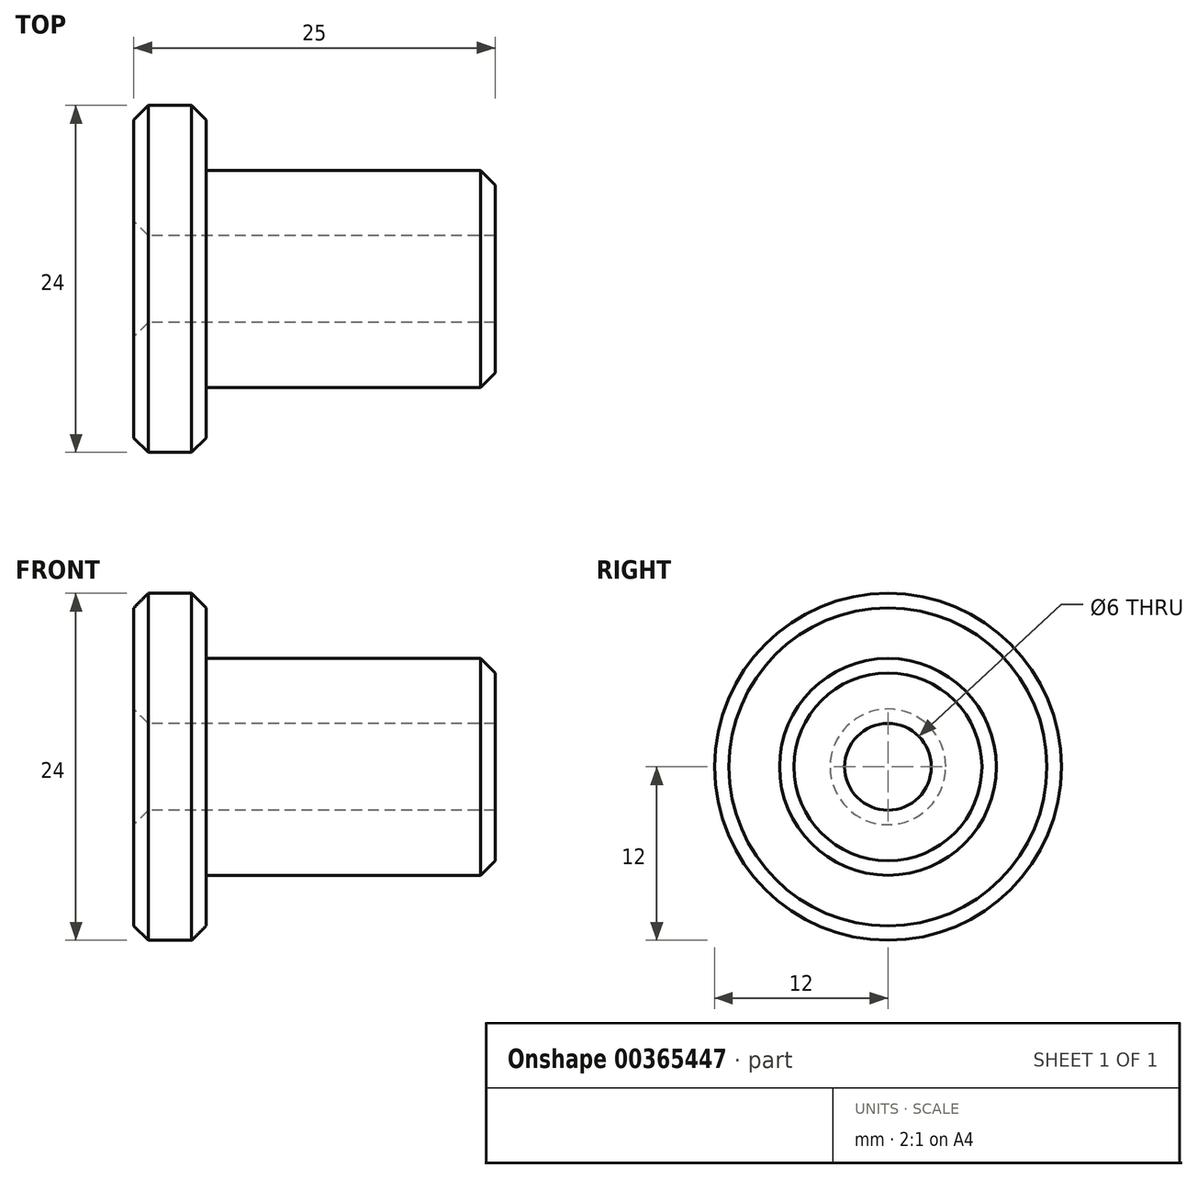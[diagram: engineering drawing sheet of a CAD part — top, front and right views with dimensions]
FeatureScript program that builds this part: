
annotation { "Feature Type Name" : "Feature", "Feature Type Description" : "" }
export const myFeature = defineFeature(function(context is Context, id is Id, definition is map)
    precondition{}
    {
        {
            var Q0;
            Q0=qCreatedBy(makeId("Front.planeOp"),FACE);
            var sketch = newSketch(context, id + "F0", { "sketchPlane" : qUnion([Q0])});
            skLineSegment(sketch, "E0", {"start": v(0, 3) * mm, "end": v(-25, 3) * mm});
            skLineSegment(sketch, "E1", {"start": v(-25, 3) * mm, "end": v(-25, 12) * mm});
            skLineSegment(sketch, "E2", {"start": v(-25, 12) * mm, "end": v(-20, 12) * mm});
            skLineSegment(sketch, "E3", {"start": v(-20, 12) * mm, "end": v(-20, 7.5) * mm});
            skLineSegment(sketch, "E4", {"start": v(-20, 7.5) * mm, "end": v(0, 7.5) * mm});
            skLineSegment(sketch, "E5", {"start": v(0, 7.5) * mm, "end": v(0, 3) * mm});
            skLineSegment(sketch, "E6", {"start": v(-45.16, 0) * mm, "end": v(21.51, 0) * mm, "construction": true});
            skSolve(sketch);
        }
        {
            var Q0;
            Q0 = qSketchRegion(id + "F0", true);
            var Q1;
            Q1=sQuery(id+"F0.wireOp",EDGE,"E6");
            revolve(context, id + "F1", {"entities" : qUnion([Q0]), "axis" : qUnion([Q1]), "revolveType" : RevolveType.FULL});
        }
        {
            var Q0;
            Q0=makeQuery(id+"F1.opRevolve","SWEPT_EDGE",EDGE,{"disambiguationData":[OSD([sQuery(id+"F0.wireOp",EDGE,"E4"),sQuery(id+"F0.wireOp",EDGE,"E5")])]});
            var Q1;
            Q1=makeQuery(id+"F1.opRevolve","SWEPT_EDGE",EDGE,{"disambiguationData":[OSD([sQuery(id+"F0.wireOp",EDGE,"E1"),sQuery(id+"F0.wireOp",EDGE,"E2")])]});
            var Q2;
            Q2=makeQuery(id+"F1.opRevolve","SWEPT_EDGE",EDGE,{"disambiguationData":[OSD([sQuery(id+"F0.wireOp",EDGE,"E2"),sQuery(id+"F0.wireOp",EDGE,"E3")])]});
            var Q3;
            Q3=makeQuery(id+"F1.opRevolve","SWEPT_EDGE",EDGE,{"disambiguationData":[OSD([sQuery(id+"F0.wireOp",EDGE,"E0"),sQuery(id+"F0.wireOp",EDGE,"E1")])]});
            chamfer(context, id + "F2", {"entities" : qUnion([Q0, Q1, Q2, Q3]), "width" : 1 * mm, "tangentPropagation" : true});
        }
    });
